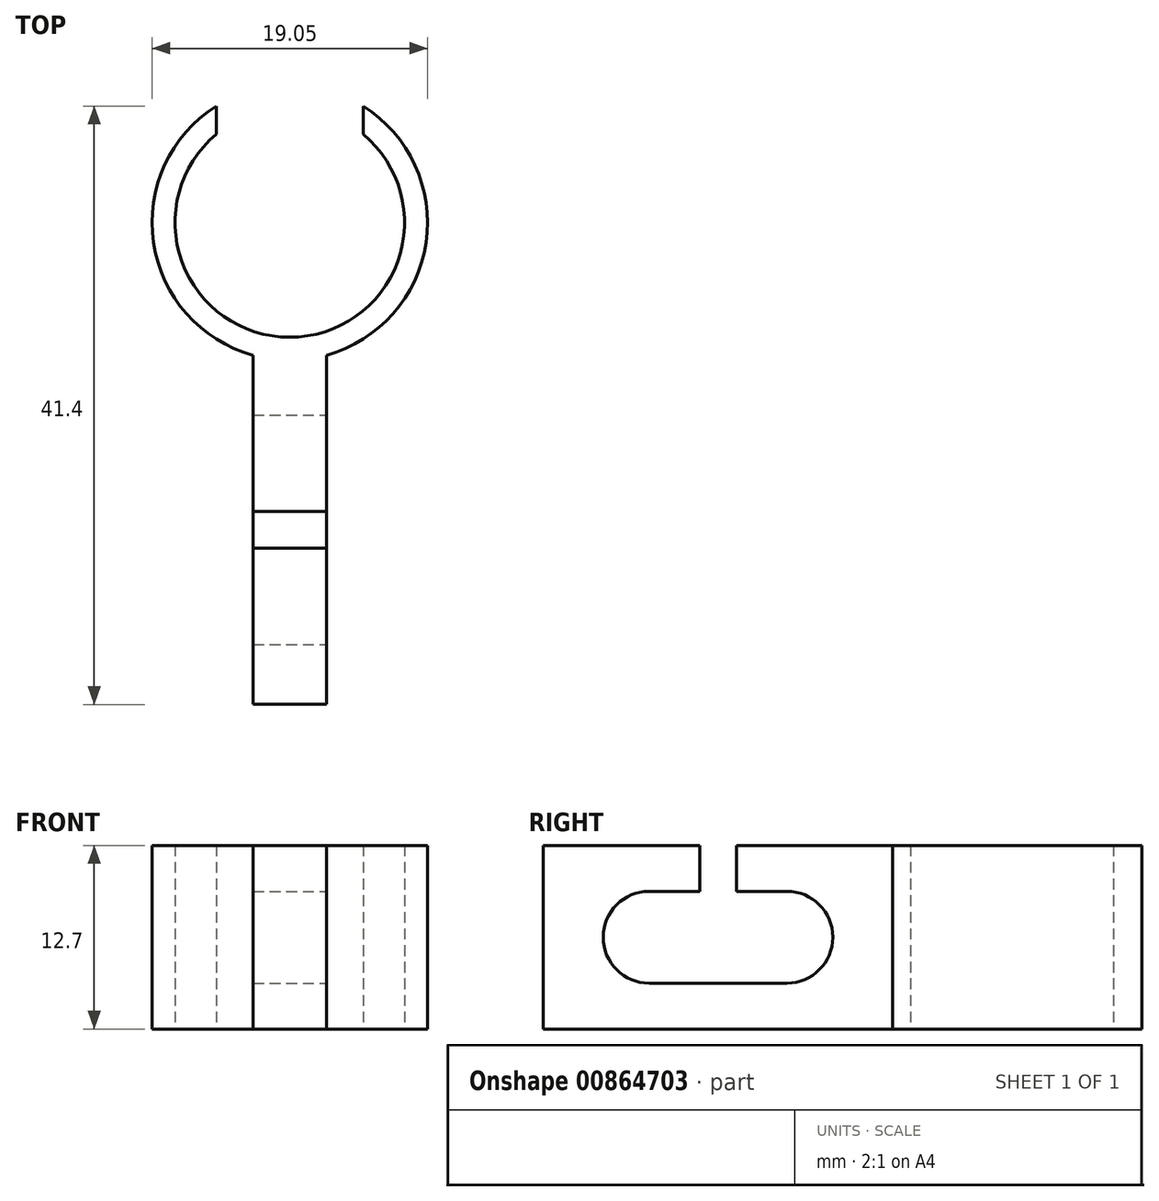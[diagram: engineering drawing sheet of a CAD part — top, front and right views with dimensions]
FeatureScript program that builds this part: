
annotation { "Feature Type Name" : "Feature", "Feature Type Description" : "" }
export const myFeature = defineFeature(function(context is Context, id is Id, definition is map)
    precondition{}
    {
        {
            var Q0;
            Q0=qCreatedBy(makeId("Top.planeOp"),FACE);
            var sketch = newSketch(context, id + "F0", { "sketchPlane" : qUnion([Q0])});
            skArc(sketch, "E0", {"start": v(-5.08, 8.06) * mm, "mid": v(0, -9.53) * mm, "end": v(5.08, 8.06) * mm});
            skArc(sketch, "E1", {"start": v(-5.08, 6.1) * mm, "mid": v(0, -7.94) * mm, "end": v(5.08, 6.1) * mm});
            skLineSegment(sketch, "E2", {"start": v(0, 0) * mm, "end": v(0, 9.53) * mm, "construction": true});
            skLineSegment(sketch, "E3.0", {"start": v(5.08, 6.1) * mm, "end": v(5.08, 8.06) * mm});
            skLineSegment(sketch, "E4.0", {"start": v(-5.08, 6.1) * mm, "end": v(-5.08, 8.06) * mm});
            skSolve(sketch);
        }
        {
            var Q0;
            Q0 = qSketchRegion(id + "F0", true);
            extrude(context, id + "F1", {"entities" : qUnion([Q0]), "depth" : 12.7 * mm, "offsetDistance" : 25.4 * mm});
        }
        {
            var Q0;
            Q0=makeQuery(id+"F1.opExtrude","CAP_FACE",FACE,{"disambiguationData":[OSD([sQuery(id+"F0.wireOp",EDGE,"E0"),sQuery(id+"F0.wireOp",EDGE,"E1"),sQuery(id+"F0.wireOp",EDGE,"E3.0"),sQuery(id+"F0.wireOp",EDGE,"E4.0")])],"isStart":false});
            var sketch = newSketch(context, id + "F2", { "sketchPlane" : qUnion([Q0])});
            skLineSegment(sketch, "E5", {"start": v(0, -7.94) * mm, "end": v(0, -9.53) * mm, "construction": true});
            skLineSegment(sketch, "E6.0", {"start": v(-2.54, -9.18) * mm, "end": v(-2.54, -33.34) * mm});
            skLineSegment(sketch, "E7.0", {"start": v(2.54, -9.18) * mm, "end": v(2.54, -33.34) * mm});
            skLineSegment(sketch, "E8", {"start": v(-2.54, -33.34) * mm, "end": v(2.54, -33.34) * mm});
            skPoint(sketch, "E9.orphan", {"position": v(-5.08, 6.1) * mm});
            skPoint(sketch, "E10.orphan", {"position": v(5.08, 6.1) * mm});
            skArc(sketch, "E11.0", {"start": v(-5.08, 8.06) * mm, "mid": v(0, -9.52) * mm, "end": v(5.08, 8.06) * mm});
            skSolve(sketch);
        }
        {
            var Q0;
            Q0 = qSketchRegion(id + "F2", true);
            var Q1;
            Q1=makeQuery(id+"F1.opExtrude","CAP_FACE",FACE,{"disambiguationData":[OSD([sQuery(id+"F0.wireOp",EDGE,"E0"),sQuery(id+"F0.wireOp",EDGE,"E1"),sQuery(id+"F0.wireOp",EDGE,"E3.0"),sQuery(id+"F0.wireOp",EDGE,"E4.0")])],"isStart":true});
            extrude(context, id + "F3", {"entities" : qUnion([Q0]), "operationType" : NewBodyOperationType.ADD, "endBound" : BoundingType.UP_TO_SURFACE, "oppositeDirection" : true, "depth" : 25.4 * mm, "endBoundEntityFace" : qUnion([Q1]), "offsetDistance" : 25.4 * mm});
        }
        {
            var Q0;
            Q0=makeQuery(id+"F3.opExtrude","SWEPT_FACE",FACE,{"disambiguationData":[OSD([sQuery(id+"F2.wireOp",EDGE,"E7.0")])]});
            var sketch = newSketch(context, id + "F4", { "sketchPlane" : qUnion([Q0])});
            skLineSegment(sketch, "E12", {"start": v(-21.26, 12.7) * mm, "end": v(-21.26, 0) * mm, "construction": true});
            skLineSegment(sketch, "E13", {"start": v(-33.34, 6.35) * mm, "end": v(-21.26, 6.35) * mm, "construction": true});
            skArc(sketch, "E14", {"start": v(-26.02, 9.53) * mm, "mid": v(-29.2, 6.35) * mm, "end": v(-26.02, 3.18) * mm});
            skArc(sketch, "E15", {"start": v(-16.49, 3.18) * mm, "mid": v(-13.31, 6.35) * mm, "end": v(-16.49, 9.53) * mm});
            skLineSegment(sketch, "E16", {"start": v(-26.02, 9.52) * mm, "end": v(-16.49, 9.53) * mm});
            skLineSegment(sketch, "E17", {"start": v(-26.02, 3.17) * mm, "end": v(-16.49, 3.17) * mm});
            skSolve(sketch);
        }
        {
            var Q0;
            Q0 = qSketchRegion(id + "F4", true);
            extrude(context, id + "F5", {"entities" : qUnion([Q0]), "operationType" : NewBodyOperationType.REMOVE, "endBound" : BoundingType.UP_TO_NEXT, "oppositeDirection" : true, "depth" : 25.4 * mm, "offsetDistance" : 25.4 * mm});
        }
        {
            var Q0;
            Q0=makeQuery(id+"F3.boolean.opBoolean","MERGE",FACE,{"derivedFrom":[makeQuery(id+"F1.opExtrude","CAP_FACE",FACE,{"disambiguationData":[OSD([sQuery(id+"F0.wireOp",EDGE,"E0"),sQuery(id+"F0.wireOp",EDGE,"E1"),sQuery(id+"F0.wireOp",EDGE,"E3.0"),sQuery(id+"F0.wireOp",EDGE,"E4.0")])],"isStart":false}),makeQuery(id+"F3.opExtrude","CAP_FACE",FACE,{"disambiguationData":[OSD([sQuery(id+"F2.wireOp",EDGE,"E6.0"),sQuery(id+"F2.wireOp",EDGE,"E7.0"),sQuery(id+"F2.wireOp",EDGE,"E8"),sQuery(id+"F2.wireOp",EDGE,"E11.0")])],"isStart":true})]});
            var sketch = newSketch(context, id + "F6", { "sketchPlane" : qUnion([Q0])});
            skLineSegment(sketch, "E18", {"start": v(-2.54, -21.26) * mm, "end": v(2.54, -21.26) * mm, "construction": true});
            skLineSegment(sketch, "E19.0", {"start": v(-2.54, -22.53) * mm, "end": v(2.54, -22.53) * mm});
            skLineSegment(sketch, "E20.0", {"start": v(-2.54, -19.99) * mm, "end": v(2.54, -19.99) * mm});
            skLineSegment(sketch, "E21", {"start": v(2.54, -19.99) * mm, "end": v(2.54, -22.53) * mm});
            skLineSegment(sketch, "E22", {"start": v(-2.54, -19.99) * mm, "end": v(-2.54, -22.53) * mm});
            skSolve(sketch);
        }
        {
            var Q0;
            Q0 = qSketchRegion(id + "F6", true);
            extrude(context, id + "F7", {"entities" : qUnion([Q0]), "operationType" : NewBodyOperationType.REMOVE, "endBound" : BoundingType.UP_TO_NEXT, "oppositeDirection" : true, "depth" : 25.4 * mm, "offsetDistance" : 25.4 * mm});
        }
    });
